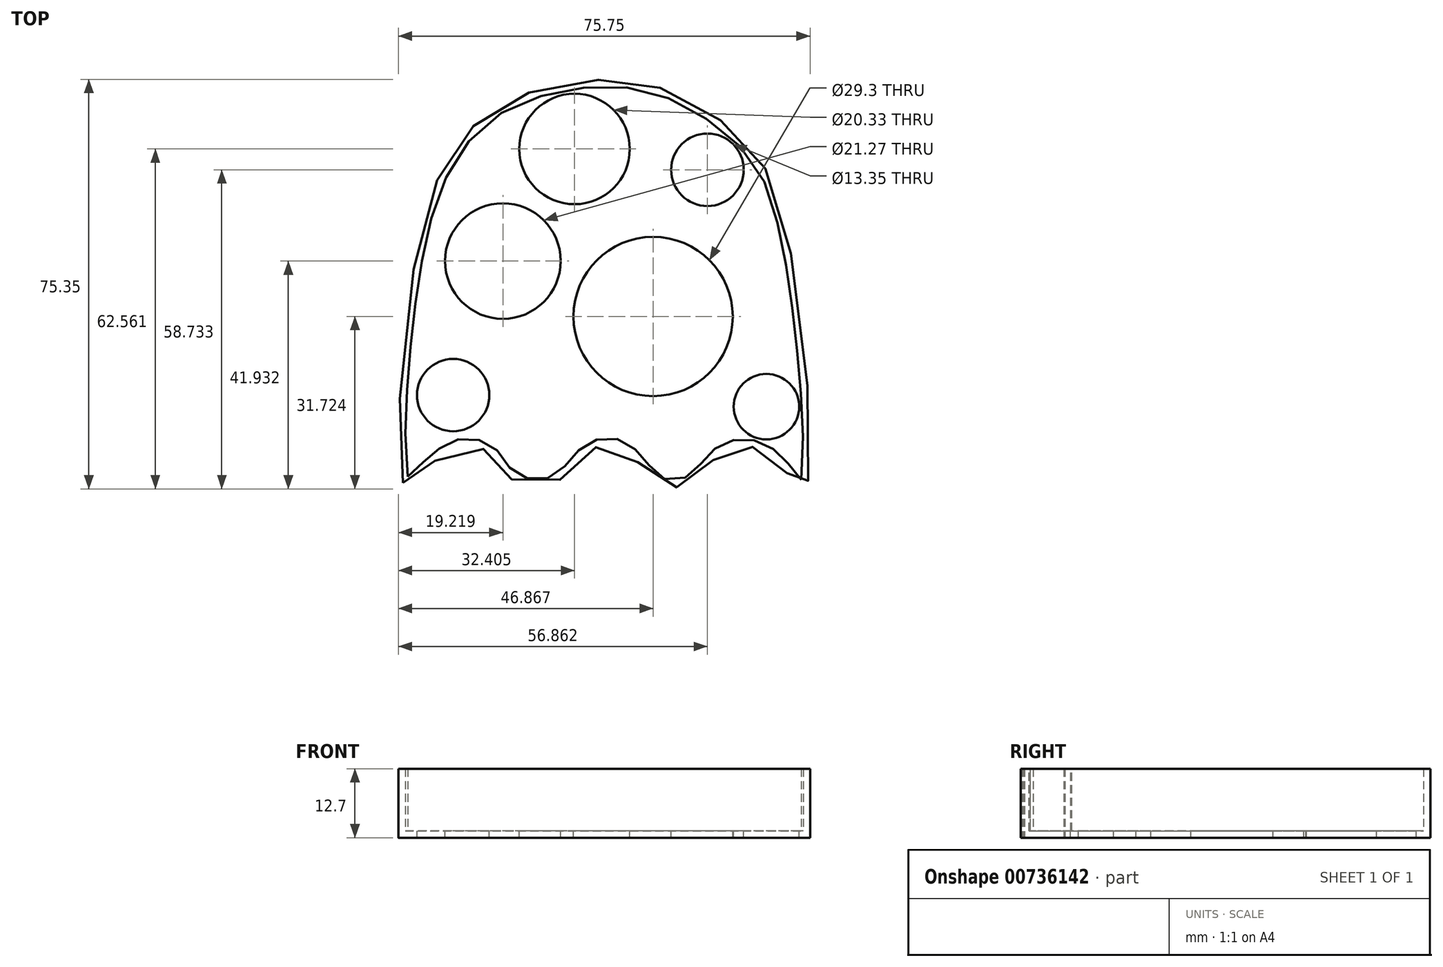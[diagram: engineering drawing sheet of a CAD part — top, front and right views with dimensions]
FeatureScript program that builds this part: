
annotation { "Feature Type Name" : "Feature", "Feature Type Description" : "" }
export const myFeature = defineFeature(function(context is Context, id is Id, definition is map)
    precondition{}
    {
        {
            var Q0;
            Q0=qCreatedBy(makeId("Top.planeOp"),FACE);
            var sketch = newSketch(context, id + "F0", { "sketchPlane" : qUnion([Q0])});
            skFitSpline(sketch, "E0", {"points": [v(-38.15, -46.27) * mm, v(-36.24, -7.37) * mm, v(-28.63, 15.26) * mm, v(-18.48, 24.14) * mm, v(-2.2, 27.94) * mm, v(10.91, 25.83) * mm, v(24.44, 16.95) * mm, v(32.48, 0) * mm, v(36.5, -45.43) * mm, v(35.23, -47.33) * mm, v(31.63, -43.31) * mm, v(26.56, -39.72) * mm, v(20.64, -40.56) * mm, v(15.35, -45.85) * mm, v(9, -46.49) * mm, v(2.66, -40.14) * mm, v(-3.9, -40.35) * mm, v(-9.81, -46.06) * mm, v(-18.06, -45.64) * mm, v(-21.65, -41.2) * mm, v(-28.42, -39.72) * mm, v(-36.66, -46.27) * mm, v(-38.15, -46.27) * mm]});
            skSolve(sketch);
        }
        {
            var Q0;
            Q0=makeQuery(id+"F0.imprint","IMPRINT",FACE,{"disambiguationData":[TD([[makeQuery(id+"F0.imprint","IMPRINT",EDGE,{"derivedFrom":sQuery(id+"F0.wireOp",EDGE,"E0")}),-1.0]])]});
            extrude(context, id + "F1", {"entities" : qUnion([Q0]), "depth" : 12.7 * mm, "offsetDistance" : 25.4 * mm});
        }
        {
            var Q0;
            Q0=makeQuery(id+"F1.opExtrude","CAP_FACE",FACE,{"disambiguationData":[OSD([sQuery(id+"F0.wireOp",EDGE,"E0")])],"isStart":false});
            shell(context, id + "F2", {"entities" : qUnion([Q0]), "thickness" : 1.27 * mm});
        }
        {
            var Q0;
            {var subQ0=sQuery(id+"F0.wireOp",EDGE,"E0");Q0=makeQuery(id+"F2.opShell","OFFSET_FACE",FACE,{"disambiguationData":[OSD([subQ0]),TDD([makeQuery(id+"F1.opExtrude","CAP_FACE",FACE,{"disambiguationData":[OSD([subQ0])],"isStart":true})])]});}
            var sketch = newSketch(context, id + "F3", { "sketchPlane" : qUnion([Q0])});
            skCircle(sketch, "E1", {"center": v(7.92, -15.64) * mm, "radius": 14.65 * mm});
            skCircle(sketch, "E2", {"center": v(-6.55, 15.2) * mm, "radius": 10.17 * mm});
            skCircle(sketch, "E3", {"center": v(-28.88, -30.1) * mm, "radius": 6.66 * mm});
            skCircle(sketch, "E4", {"center": v(-19.73, -5.43) * mm, "radius": 10.63 * mm});
            skCircle(sketch, "E5", {"center": v(17.91, 11.37) * mm, "radius": 6.67 * mm});
            skCircle(sketch, "E6", {"center": v(28.76, -32.23) * mm, "radius": 6.02 * mm});
            skSolve(sketch);
        }
        {
            var Q0;
            Q0 = qSketchRegion(id + "F3", true);
            extrude(context, id + "F4", {"entities" : qUnion([Q0]), "operationType" : NewBodyOperationType.REMOVE, "oppositeDirection" : true, "depth" : 25.4 * mm, "offsetDistance" : 25.4 * mm});
        }
    });
